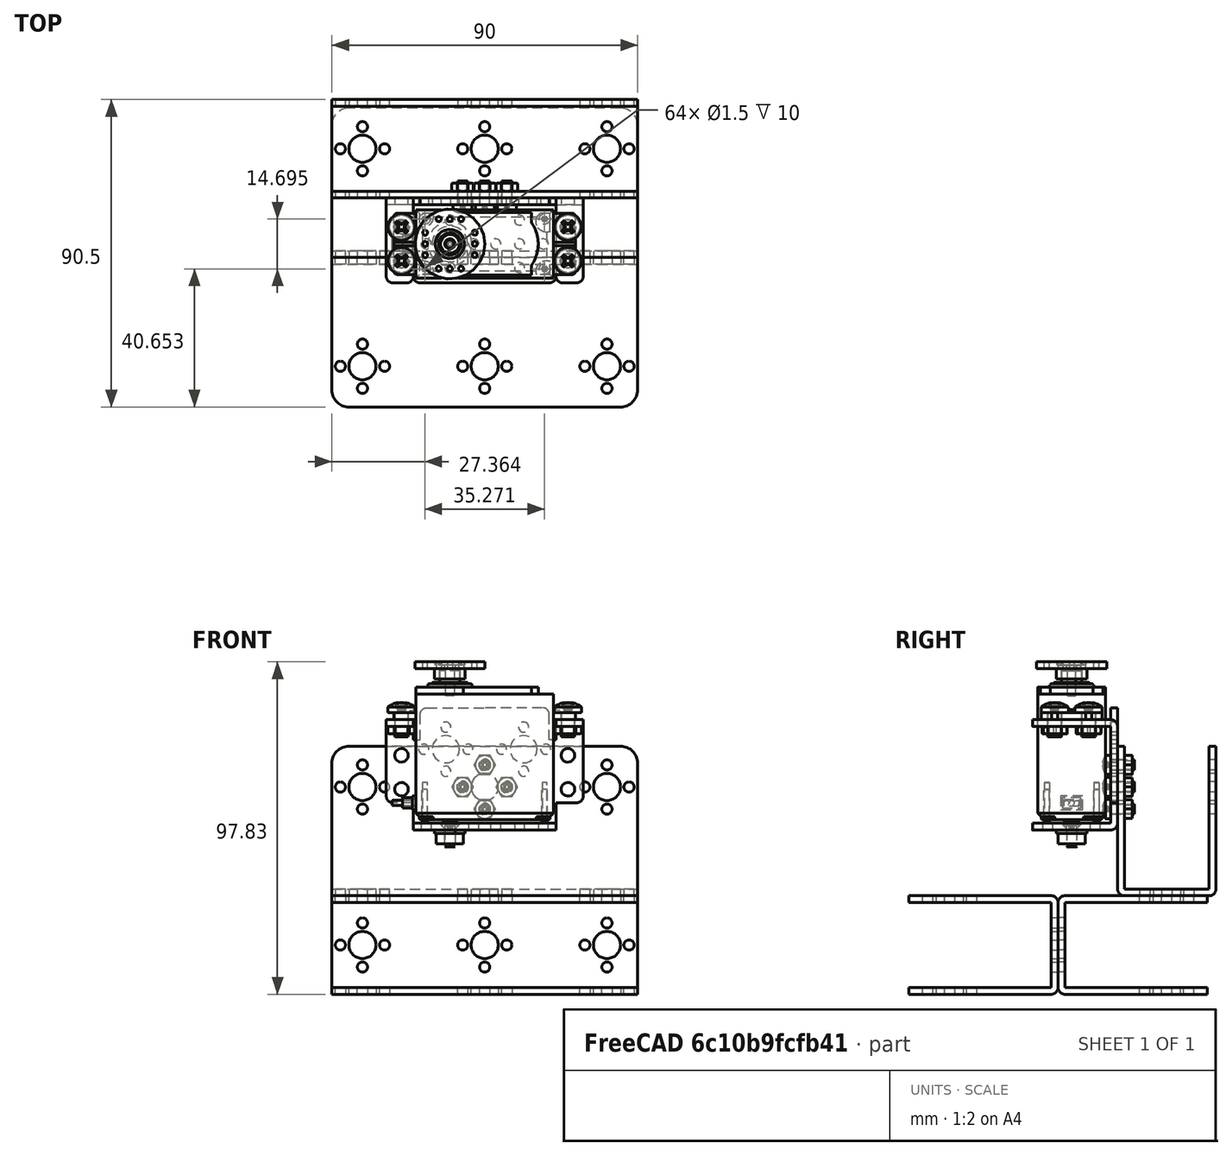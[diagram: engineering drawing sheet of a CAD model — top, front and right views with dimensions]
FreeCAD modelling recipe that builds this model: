
FCSTD DOCUMENT  (FreeCAD 0.19R24276 (Git))
Label: base
License: All rights reserved
LicenseURL: http://en.wikipedia.org/wiki/All_rights_reserved
objects: App::FeaturePython×18, Part::FeaturePython×8
note: 8 computed .brp shape members not serialized (recipe doc carries the construction recipe); baked Part::Feature solids carry a one-line shape summary decoded from their .brp

FEATURE [Part::FeaturePython] b_parte_baja_001_  label="parte_baja_001"  # a2plus imported part (geometry in sourceFile) (typed FeaturePython)
  Placement = pos=(0,0,0) rot=(1,0,0;1.5708rad)
  a2p_Version = V0.1
  fixedPosition = true
  objectType = a2pPart
  sourceFile = .\..\piezas\parte_baja.FCStd
  subassemblyImport = false
  timeLastImport = 1.62041e+09
  updateColors = true
FEATURE [Part::FeaturePython] b_parte_baja_001_001  label="parte_baja_002"  # a2plus imported part (geometry in sourceFile) (typed FeaturePython)
  Placement = pos=(2e-15,0,-2.90989e-08) rot=(-1,0,0;1.5708rad)
  a2p_Version = V0.1
  fixedPosition = false
  objectType = a2pPart
  sourceFile = .\..\piezas\parte_baja.FCStd
  subassemblyImport = false
  timeLastImport = 1.62041e+09
  updateColors = true
FEATURE [Part::FeaturePython] b_parte_baja_001_002  label="parte_baja_003"  # a2plus imported part (geometry in sourceFile) (typed FeaturePython)
  Placement = pos=(0,32,14.5) rot=(0,0,1;0rad)
  a2p_Version = V0.1
  fixedPosition = false
  objectType = a2pPart
  sourceFile = .\..\piezas\parte_baja.FCStd
  subassemblyImport = false
  timeLastImport = 1.62041e+09
  updateColors = true
FEATURE [App::FeaturePython] planeCoincident_001  label="planeCoincident_001__parte_baja_002"  # a2plus constraint (typed FeaturePython)
  Object1 = b_parte_baja_001_
  Object2 = b_parte_baja_001_001
  ParentTreeObject = -> b_parte_baja_001_
  SubElement1 = Face28
  SubElement2 = Face28
  Suppressed = false
  Type = plane
  directionConstraint = 1
  offset = 0
FEATURE [App::FeaturePython] planeCoincident_001_mirror  label="planeCoincident_001__parte_baja_001"  # a2plus constraint (typed FeaturePython)
  Object1 = b_parte_baja_001_
  Object2 = b_parte_baja_001_001
  ParentTreeObject = -> b_parte_baja_001_001
  SubElement1 = Face28
  SubElement2 = Face28
  Suppressed = false
  Type = plane
  directionConstraint = 1
  offset = 0
FEATURE [App::FeaturePython] axisCoincident_001  label="axisCoincident_001__parte_baja_002"  # a2plus constraint (typed FeaturePython)
  Object1 = b_parte_baja_001_
  Object2 = b_parte_baja_001_001
  ParentTreeObject = -> b_parte_baja_001_
  SubElement1 = Face45
  SubElement2 = Face45
  Suppressed = false
  Type = axial
  directionConstraint = 1
  lockRotation = false
FEATURE [App::FeaturePython] axisCoincident_001_mirror  label="axisCoincident_001__parte_baja_001"  # a2plus constraint (typed FeaturePython)
  Object1 = b_parte_baja_001_
  Object2 = b_parte_baja_001_001
  ParentTreeObject = -> b_parte_baja_001_001
  SubElement1 = Face45
  SubElement2 = Face45
  Suppressed = false
  Type = axial
  directionConstraint = 1
  lockRotation = false
FEATURE [App::FeaturePython] axisCoincident_002  label="axisCoincident_002__parte_baja_002"  # a2plus constraint (typed FeaturePython)
  Object1 = b_parte_baja_001_
  Object2 = b_parte_baja_001_001
  ParentTreeObject = -> b_parte_baja_001_
  SubElement1 = Face39
  SubElement2 = Face39
  Suppressed = false
  Type = axial
  directionConstraint = 1
  lockRotation = false
FEATURE [App::FeaturePython] axisCoincident_002_mirror  label="axisCoincident_002__parte_baja_001"  # a2plus constraint (typed FeaturePython)
  Object1 = b_parte_baja_001_
  Object2 = b_parte_baja_001_001
  ParentTreeObject = -> b_parte_baja_001_001
  SubElement1 = Face39
  SubElement2 = Face39
  Suppressed = false
  Type = axial
  directionConstraint = 1
  lockRotation = false
FEATURE [App::FeaturePython] planeCoincident_002  label="planeCoincident_002__parte_baja_002"  # a2plus constraint (typed FeaturePython)
  Object1 = b_parte_baja_001_002
  Object2 = b_parte_baja_001_001
  ParentTreeObject = -> b_parte_baja_001_002
  SubElement1 = Face28
  SubElement2 = Face49
  Suppressed = false
  Type = plane
  directionConstraint = 0
  offset = 0
FEATURE [App::FeaturePython] planeCoincident_002_mirror  label="planeCoincident_002__parte_baja_003"  # a2plus constraint (typed FeaturePython)
  Object1 = b_parte_baja_001_002
  Object2 = b_parte_baja_001_001
  ParentTreeObject = -> b_parte_baja_001_001
  SubElement1 = Face28
  SubElement2 = Face49
  Suppressed = false
  Type = plane
  directionConstraint = 0
  offset = 0
FEATURE [App::FeaturePython] axisCoincident_003  label="axisCoincident_003__parte_baja_003"  # a2plus constraint (typed FeaturePython)
  Object1 = b_parte_baja_001_001
  Object2 = b_parte_baja_001_002
  ParentTreeObject = -> b_parte_baja_001_001
  SubElement1 = Face64
  SubElement2 = Face45
  Suppressed = false
  Type = axial
  directionConstraint = 1
  lockRotation = false
FEATURE [App::FeaturePython] axisCoincident_003_mirror  label="axisCoincident_003__parte_baja_002"  # a2plus constraint (typed FeaturePython)
  Object1 = b_parte_baja_001_001
  Object2 = b_parte_baja_001_002
  ParentTreeObject = -> b_parte_baja_001_002
  SubElement1 = Face64
  SubElement2 = Face45
  Suppressed = false
  Type = axial
  directionConstraint = 1
  lockRotation = false
FEATURE [App::FeaturePython] axisCoincident_004  label="axisCoincident_004__parte_baja_003"  # a2plus constraint (typed FeaturePython)
  Object1 = b_parte_baja_001_001
  Object2 = b_parte_baja_001_002
  ParentTreeObject = -> b_parte_baja_001_001
  SubElement1 = Face59
  SubElement2 = Face39
  Suppressed = false
  Type = axial
  directionConstraint = 1
  lockRotation = false
FEATURE [App::FeaturePython] axisCoincident_004_mirror  label="axisCoincident_004__parte_baja_002"  # a2plus constraint (typed FeaturePython)
  Object1 = b_parte_baja_001_001
  Object2 = b_parte_baja_001_002
  ParentTreeObject = -> b_parte_baja_001_002
  SubElement1 = Face59
  SubElement2 = Face39
  Suppressed = false
  Type = axial
  directionConstraint = 1
  lockRotation = false
FEATURE [Part::FeaturePython] b_servo_acoplado_1_001_  label="servo_acoplado_1_001"  # a2plus imported part (geometry in sourceFile) (typed FeaturePython)
  Placement = pos=(3.84178e-07,4,36.8289) rot=(0,0,1;0rad)
  a2p_Version = V0.1
  fixedPosition = false
  objectType = a2pPart
  sourceFile = .\servo_acoplado_1.FCStd
  subassemblyImport = false
  timeLastImport = 1.62041e+09
  updateColors = true
FEATURE [App::FeaturePython] planeCoincident_003  label="planeCoincident_003__parte_baja_003"  # a2plus constraint (typed FeaturePython)
  Object1 = b_servo_acoplado_1_001_
  Object2 = b_parte_baja_001_002
  ParentTreeObject = -> b_servo_acoplado_1_001_
  SubElement1 = Face68
  SubElement2 = Face49
  Suppressed = false
  Type = plane
  directionConstraint = 1
  offset = 0
FEATURE [App::FeaturePython] planeCoincident_003_mirror  label="planeCoincident_003__servo_acoplado_1_001"  # a2plus constraint (typed FeaturePython)
  Object1 = b_servo_acoplado_1_001_
  Object2 = b_parte_baja_001_002
  ParentTreeObject = -> b_parte_baja_001_002
  SubElement1 = Face68
  SubElement2 = Face49
  Suppressed = false
  Type = plane
  directionConstraint = 1
  offset = 0
FEATURE [App::FeaturePython] axisCoincident_005  label="axisCoincident_005__parte_baja_003"  # a2plus constraint (typed FeaturePython)
  Object1 = b_servo_acoplado_1_001_
  Object2 = b_parte_baja_001_002
  ParentTreeObject = -> b_servo_acoplado_1_001_
  SubElement1 = Face3316
  SubElement2 = Face55
  Suppressed = false
  Type = axial
  directionConstraint = 1
  lockRotation = false
FEATURE [App::FeaturePython] axisCoincident_005_mirror  label="axisCoincident_005__servo_acoplado_1_001"  # a2plus constraint (typed FeaturePython)
  Object1 = b_servo_acoplado_1_001_
  Object2 = b_parte_baja_001_002
  ParentTreeObject = -> b_parte_baja_001_002
  SubElement1 = Face3316
  SubElement2 = Face55
  Suppressed = false
  Type = axial
  directionConstraint = 1
  lockRotation = false
FEATURE [App::FeaturePython] axisCoincident_006  label="axisCoincident_006__parte_baja_003"  # a2plus constraint (typed FeaturePython)
  Object1 = b_servo_acoplado_1_001_
  Object2 = b_parte_baja_001_002
  ParentTreeObject = -> b_servo_acoplado_1_001_
  SubElement1 = Face3132
  SubElement2 = Face66
  Suppressed = false
  Type = axial
  directionConstraint = 1
  lockRotation = false
FEATURE [App::FeaturePython] axisCoincident_006_mirror  label="axisCoincident_006__servo_acoplado_1_001"  # a2plus constraint (typed FeaturePython)
  Object1 = b_servo_acoplado_1_001_
  Object2 = b_parte_baja_001_002
  ParentTreeObject = -> b_parte_baja_001_002
  SubElement1 = Face3132
  SubElement2 = Face66
  Suppressed = false
  Type = axial
  directionConstraint = 1
  lockRotation = false
FEATURE [Part::FeaturePython] Nut  label="M3-Nut"  # Fasteners workbench fastener (typed FeaturePython)
  Placement = pos=(0,19.5,53) rot=(-1,0,0;1.5708rad)
  baseObject = -> b_parte_baja_001_002 [Edge125]
  diameter = 4
  invert = true
  matchOuter = true
  offset = 0
  thread = false
  type = 7
FEATURE [Part::FeaturePython] Nut001  label="M3-Nut001"  # Fasteners workbench fastener (typed FeaturePython)
  Placement = pos=(6.5,19.5,46.5) rot=(-1,0,0;1.5708rad)
  baseObject = -> b_parte_baja_001_002 [Edge130]
  diameter = 4
  invert = true
  matchOuter = true
  offset = 0
  thread = false
  type = 7
FEATURE [Part::FeaturePython] Nut002  label="M3-Nut002"  # Fasteners workbench fastener (typed FeaturePython)
  Placement = pos=(0,19.5,40) rot=(-1,0,0;1.5708rad)
  baseObject = -> b_parte_baja_001_002 [Edge136]
  diameter = 4
  invert = true
  matchOuter = true
  offset = 0
  thread = false
  type = 7
FEATURE [Part::FeaturePython] Nut003  label="M3-Nut003"  # Fasteners workbench fastener (typed FeaturePython)
  Placement = pos=(-6.5,19.5,46.5) rot=(-1,0,0;1.5708rad)
  baseObject = -> b_parte_baja_001_002 [Edge133]
  diameter = 4
  invert = true
  matchOuter = true
  offset = 0
  thread = false
  type = 7
